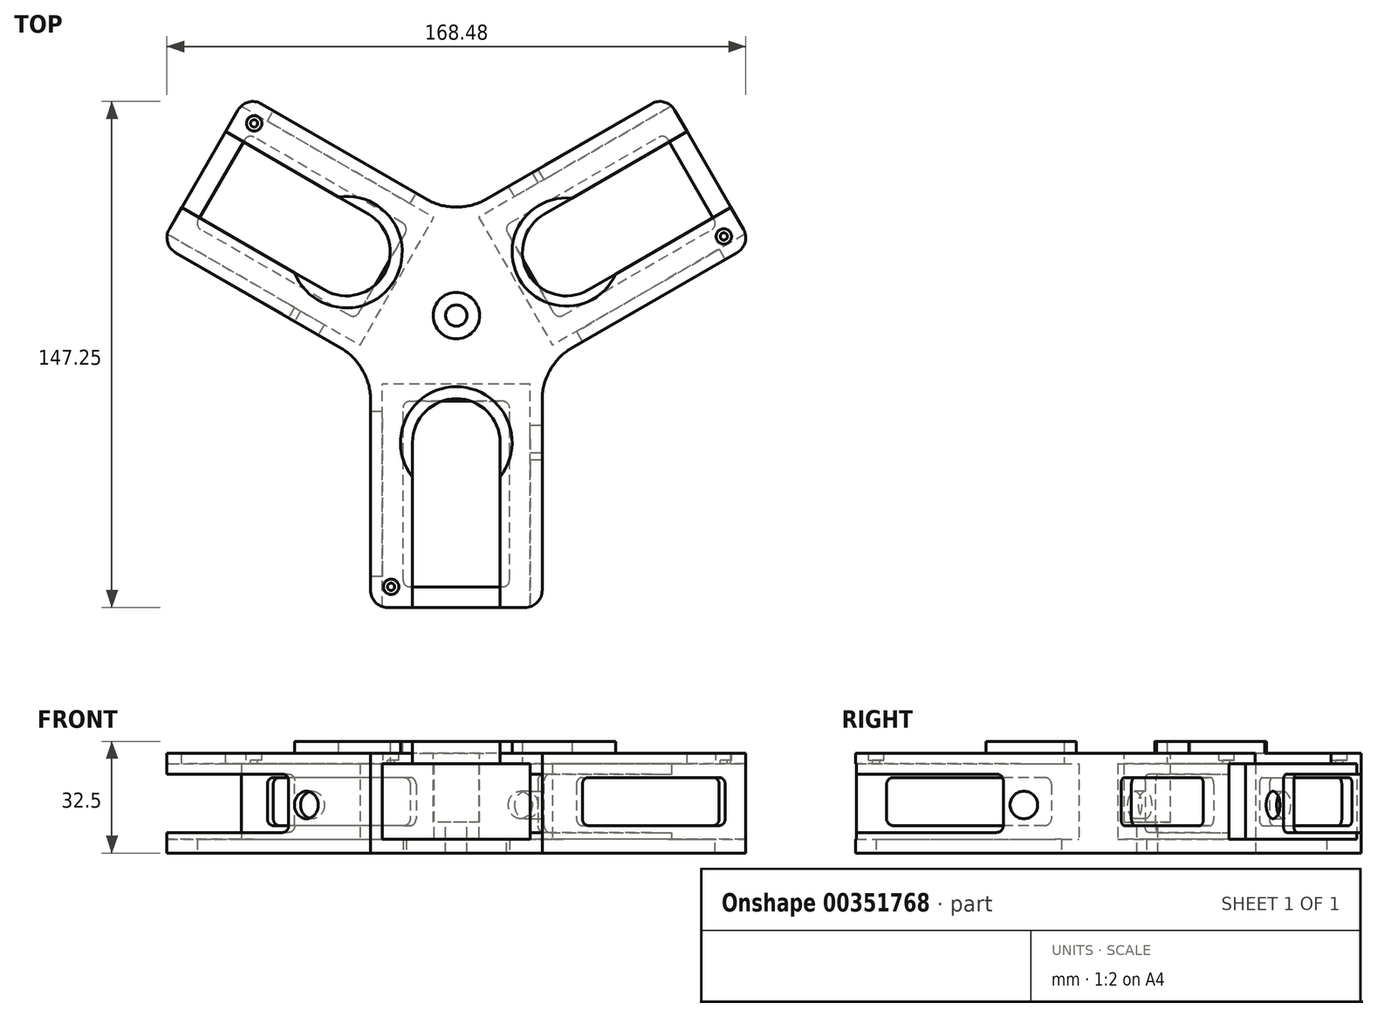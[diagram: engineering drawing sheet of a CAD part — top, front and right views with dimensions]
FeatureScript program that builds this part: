
annotation { "Feature Type Name" : "Feature", "Feature Type Description" : "" }
export const myFeature = defineFeature(function(context is Context, id is Id, definition is map)
    precondition{}
    {
        {
            var Q0;
            Q0=qCreatedBy(makeId("Top.planeOp"),FACE);
            var sketch = newSketch(context, id + "F0", { "sketchPlane" : qUnion([Q0])});
            skCircle(sketch, "E0.cCircle", {"center": v(0, 0) * mm, "radius": 18.48 * mm, "construction": true});
            skLineSegment(sketch, "E0.0", {"start": v(-32, 18.48) * mm, "end": v(32, 18.48) * mm, "construction": true});
            skLineSegment(sketch, "E0.1", {"start": v(32, 18.48) * mm, "end": v(0, -36.95) * mm, "construction": true});
            skLineSegment(sketch, "E0.2", {"start": v(0, -36.95) * mm, "end": v(-32, 18.48) * mm, "construction": true});
            skPoint(sketch, "E0.0.midPoint", {"position": v(0, 18.48) * mm});
            skLineSegment(sketch, "E1.bottom", {"start": v(21.5, -84.95) * mm, "end": v(-21.5, -84.95) * mm});
            skLineSegment(sketch, "E1.top", {"start": v(21.5, -19.95) * mm, "end": v(-21.5, -19.95) * mm});
            skLineSegment(sketch, "E1.left", {"start": v(21.5, -84.95) * mm, "end": v(21.5, -19.95) * mm});
            skLineSegment(sketch, "E1.right", {"start": v(-21.5, -84.95) * mm, "end": v(-21.5, -19.95) * mm});
            skPoint(sketch, "E1.middle", {"position": v(0, -52.45) * mm});
            skLineSegment(sketch, "E2.1.0", {"start": v(84.32, 23.86) * mm, "end": v(28.03, -8.64) * mm});
            skLineSegment(sketch, "E2.1.1", {"start": v(6.53, 28.6) * mm, "end": v(28.03, -8.64) * mm});
            skLineSegment(sketch, "E2.1.2", {"start": v(62.82, 61.1) * mm, "end": v(6.53, 28.6) * mm});
            skLineSegment(sketch, "E2.1.3", {"start": v(62.82, 61.1) * mm, "end": v(84.32, 23.86) * mm});
            skLineSegment(sketch, "E2.2.0", {"start": v(-62.82, 61.1) * mm, "end": v(-6.53, 28.6) * mm});
            skLineSegment(sketch, "E2.2.1", {"start": v(-28.03, -8.64) * mm, "end": v(-6.53, 28.6) * mm});
            skLineSegment(sketch, "E2.2.2", {"start": v(-84.32, 23.86) * mm, "end": v(-28.03, -8.64) * mm});
            skLineSegment(sketch, "E2.2.3", {"start": v(-84.32, 23.86) * mm, "end": v(-62.82, 61.1) * mm});
            skPoint(sketch, "E3.centerSnap0", {"position": v(0, -19.95) * mm});
            skCircle(sketch, "E4", {"center": v(0, -36.95) * mm, "radius": 12.75 * mm});
            skCircle(sketch, "E5", {"center": v(32, 18.48) * mm, "radius": 12.75 * mm});
            skCircle(sketch, "E6", {"center": v(-32, 18.48) * mm, "radius": 12.75 * mm});
            skLineSegment(sketch, "E7.0", {"start": v(61.07, 64.13) * mm, "end": v(4.78, 31.63) * mm});
            skLineSegment(sketch, "E7.2", {"start": v(86.07, 20.82) * mm, "end": v(29.78, -11.68) * mm});
            skLineSegment(sketch, "E8.0", {"start": v(-61.07, 64.13) * mm, "end": v(-4.78, 31.63) * mm});
            skLineSegment(sketch, "E8.2", {"start": v(-86.07, 20.82) * mm, "end": v(-29.78, -11.68) * mm});
            skLineSegment(sketch, "E9.0", {"start": v(25, -84.95) * mm, "end": v(25, -19.95) * mm});
            skLineSegment(sketch, "E9.2", {"start": v(-25, -84.95) * mm, "end": v(-25, -19.95) * mm});
            skLineSegment(sketch, "E10", {"start": v(4.78, 31.63) * mm, "end": v(-4.78, 31.63) * mm});
            skLineSegment(sketch, "E11", {"start": v(29.78, -11.68) * mm, "end": v(25, -19.95) * mm});
            skLineSegment(sketch, "E12", {"start": v(-29.78, -11.68) * mm, "end": v(-25, -19.95) * mm});
            skCircle(sketch, "E13", {"center": v(0, 0) * mm, "radius": 3.1 * mm});
            skLineSegment(sketch, "E14", {"start": v(-62.82, 61.1) * mm, "end": v(-61.07, 64.13) * mm});
            skLineSegment(sketch, "E15", {"start": v(-84.32, 23.86) * mm, "end": v(-86.07, 20.82) * mm});
            skLineSegment(sketch, "E16", {"start": v(-21.5, -84.95) * mm, "end": v(-25, -84.95) * mm});
            skLineSegment(sketch, "E17", {"start": v(21.5, -84.95) * mm, "end": v(25, -84.95) * mm});
            skLineSegment(sketch, "E18", {"start": v(62.82, 61.1) * mm, "end": v(61.07, 64.13) * mm});
            skLineSegment(sketch, "E19", {"start": v(84.32, 23.86) * mm, "end": v(86.07, 20.82) * mm});
            skSolve(sketch);
        }
        {
            var Q0;
            Q0=makeQuery(id+"F0.imprint","IMPRINT",FACE,{"disambiguationData":[TD([[makeQuery(id+"F0.imprint","IMPRINT",EDGE,{"derivedFrom":sQuery(id+"F0.wireOp",EDGE,"E1.top")}),-1.0]])]});
            var Q1;
            Q1=makeQuery(id+"F0.imprint","IMPRINT",FACE,{"disambiguationData":[TD([[makeQuery(id+"F0.imprint","IMPRINT",EDGE,{"derivedFrom":sQuery(id+"F0.wireOp",EDGE,"E2.2.0")}),-1.0]])]});
            var Q2;
            Q2=makeQuery(id+"F0.imprint","IMPRINT",FACE,{"disambiguationData":[TD([[makeQuery(id+"F0.imprint","IMPRINT",EDGE,{"derivedFrom":sQuery(id+"F0.wireOp",EDGE,"E6")}),1.0]])]});
            var Q3;
            Q3=makeQuery(id+"F0.imprint","IMPRINT",FACE,{"disambiguationData":[TD([[makeQuery(id+"F0.imprint","IMPRINT",EDGE,{"derivedFrom":sQuery(id+"F0.wireOp",EDGE,"E5")}),1.0]])]});
            var Q4;
            Q4=makeQuery(id+"F0.imprint","IMPRINT",FACE,{"disambiguationData":[TD([[makeQuery(id+"F0.imprint","IMPRINT",EDGE,{"derivedFrom":sQuery(id+"F0.wireOp",EDGE,"E2.1.0")}),-1.0]])]});
            var Q5;
            Q5=makeQuery(id+"F0.imprint","IMPRINT",FACE,{"disambiguationData":[TD([[makeQuery(id+"F0.imprint","IMPRINT",EDGE,{"derivedFrom":sQuery(id+"F0.wireOp",EDGE,"E1.bottom")}),-1.0]])]});
            var Q6;
            Q6=makeQuery(id+"F0.imprint","IMPRINT",FACE,{"disambiguationData":[TD([[makeQuery(id+"F0.imprint","IMPRINT",EDGE,{"derivedFrom":sQuery(id+"F0.wireOp",EDGE,"E4")}),1.0]])]});
            var Q7;
            Q7=makeQuery(id+"F0.imprint","IMPRINT",FACE,{"disambiguationData":[TD([[makeQuery(id+"F0.imprint","IMPRINT",EDGE,{"derivedFrom":sQuery(id+"F0.wireOp",EDGE,"E1.bottom")}),1.0]])]});
            var Q8;
            Q8=makeQuery(id+"F0.imprint","IMPRINT",FACE,{"disambiguationData":[TD([[makeQuery(id+"F0.imprint","IMPRINT",EDGE,{"derivedFrom":sQuery(id+"F0.wireOp",EDGE,"E2.1.3")}),1.0]])]});
            var Q9;
            Q9=makeQuery(id+"F0.imprint","IMPRINT",FACE,{"disambiguationData":[TD([[makeQuery(id+"F0.imprint","IMPRINT",EDGE,{"derivedFrom":sQuery(id+"F0.wireOp",EDGE,"E2.2.3")}),1.0]])]});
            extrude(context, id + "F1", {"entities" : qUnion([Q0, Q1, Q2, Q3, Q4, Q5, Q6, Q7, Q8, Q9]), "oppositeDirection" : true, "depth" : 4 * mm, "offsetDistance" : 25 * mm});
        }
        {
            var Q0;
            Q0=makeQuery(id+"F0.imprint","IMPRINT",FACE,{"disambiguationData":[TD([[makeQuery(id+"F0.imprint","IMPRINT",EDGE,{"derivedFrom":sQuery(id+"F0.wireOp",EDGE,"E1.top")}),-1.0]])]});
            extrude(context, id + "F2", {"entities" : qUnion([Q0]), "operationType" : NewBodyOperationType.ADD, "depth" : 25 * mm, "offsetDistance" : 25 * mm});
        }
        {
            var Q0;
            Q0=makeQuery(id+"F0.imprint","IMPRINT",FACE,{"disambiguationData":[TD([[makeQuery(id+"F0.imprint","IMPRINT",EDGE,{"derivedFrom":sQuery(id+"F0.wireOp",EDGE,"E1.bottom")}),-1.0]])]});
            var Q1;
            Q1=makeQuery(id+"F0.imprint","IMPRINT",FACE,{"disambiguationData":[TD([[makeQuery(id+"F0.imprint","IMPRINT",EDGE,{"derivedFrom":sQuery(id+"F0.wireOp",EDGE,"E2.2.0")}),-1.0]])]});
            var Q2;
            Q2=makeQuery(id+"F0.imprint","IMPRINT",FACE,{"disambiguationData":[TD([[makeQuery(id+"F0.imprint","IMPRINT",EDGE,{"derivedFrom":sQuery(id+"F0.wireOp",EDGE,"E2.1.0")}),-1.0]])]});
            extrude(context, id + "F3", {"entities" : qUnion([Q0, Q1, Q2]), "operationType" : NewBodyOperationType.ADD, "depth" : 25 * mm, "offsetDistance" : 25 * mm, "hasSecondDirection" : true, "secondDirectionOppositeDirection" : false, "secondDirectionDepth" : 22 * mm});
        }
        {
            var Q0;
            Q0=makeQuery(id+"F0.imprint","IMPRINT",FACE,{"disambiguationData":[TD([[makeQuery(id+"F0.imprint","IMPRINT",EDGE,{"derivedFrom":sQuery(id+"F0.wireOp",EDGE,"E5")}),1.0]])]});
            var Q1;
            Q1=makeQuery(id+"F0.imprint","IMPRINT",FACE,{"disambiguationData":[TD([[makeQuery(id+"F0.imprint","IMPRINT",EDGE,{"derivedFrom":sQuery(id+"F0.wireOp",EDGE,"E6")}),1.0]])]});
            var Q2;
            Q2=makeQuery(id+"F0.imprint","IMPRINT",FACE,{"disambiguationData":[TD([[makeQuery(id+"F0.imprint","IMPRINT",EDGE,{"derivedFrom":sQuery(id+"F0.wireOp",EDGE,"E4")}),1.0]])]});
            extrude(context, id + "F4", {"entities" : qUnion([Q0, Q1, Q2]), "operationType" : NewBodyOperationType.REMOVE, "depth" : 36.1 * mm, "offsetDistance" : 25 * mm, "hasSecondDirection" : true, "secondDirectionOppositeDirection" : false, "secondDirectionDepth" : 12.2 * mm});
        }
        {
            var Q0;
            {var subQ0=sQuery(id+"F0.wireOp",EDGE,"E2.2.2");var subQ1=sQuery(id+"F0.wireOp",EDGE,"E2.2.1");var subQ2=sQuery(id+"F0.wireOp",EDGE,"E2.2.0");var subQ3=sQuery(id+"F0.wireOp",EDGE,"E2.1.2");var subQ4=sQuery(id+"F0.wireOp",EDGE,"E2.1.1");var subQ5=sQuery(id+"F0.wireOp",EDGE,"E2.1.0");var subQ6=sQuery(id+"F0.wireOp",EDGE,"E1.right");var subQ7=sQuery(id+"F0.wireOp",EDGE,"E1.left");var subQ8=sQuery(id+"F0.wireOp",EDGE,"E1.top");Q0=makeQuery(id+"F3.boolean.opBoolean","MERGE",FACE,{"derivedFrom":[makeQuery(id+"F2.opExtrude","CAP_FACE",FACE,{"disambiguationData":[OSD([subQ8,subQ7,subQ6,subQ5,subQ4,subQ3,subQ2,subQ1,subQ0,sQuery(id+"F0.wireOp",EDGE,"E7.0"),sQuery(id+"F0.wireOp",EDGE,"E7.1"),sQuery(id+"F0.wireOp",EDGE,"E7.2"),sQuery(id+"F0.wireOp",EDGE,"E8.0"),sQuery(id+"F0.wireOp",EDGE,"E8.1"),sQuery(id+"F0.wireOp",EDGE,"E8.2"),sQuery(id+"F0.wireOp",EDGE,"E9.0"),sQuery(id+"F0.wireOp",EDGE,"E9.1"),sQuery(id+"F0.wireOp",EDGE,"E9.2"),sQuery(id+"F0.wireOp",EDGE,"E10"),sQuery(id+"F0.wireOp",EDGE,"E11"),sQuery(id+"F0.wireOp",EDGE,"E12"),sQuery(id+"F0.wireOp",EDGE,"jiN8x03o-aMMn-jMTH-HvWz-tqMVP37OVDIm"),sQuery(id+"F0.wireOp",EDGE,"EKPgnR2F-pnn3-6EDa-x4Kd-Pkry5YZrHWNk"),sQuery(id+"F0.wireOp",EDGE,"n5eVLuFF-JwKT-QSBh-8ASv-iFnnVuZWaxG4"),sQuery(id+"F0.wireOp",EDGE,"HnI92CDr-kPty-4Z3F-qDl1-UzYuS8kZJhd5"),sQuery(id+"F0.wireOp",EDGE,"Mza90nwJ-3rcs-2YEg-8f4p-QPBBZ3gxiD8u"),sQuery(id+"F0.wireOp",EDGE,"szRdEE3T-eoAc-AhTw-RHdj-YrhbBiVasdUm"),sQuery(id+"F0.wireOp",EDGE,"E13")])],"isStart":false}),makeQuery(id+"F3.opExtrude","CAP_FACE",FACE,{"disambiguationData":[OSD([sQuery(id+"F0.wireOp",EDGE,"E1.bottom"),subQ8,subQ7,subQ6,sQuery(id+"F0.wireOp",EDGE,"E4")])],"isStart":false}),makeQuery(id+"F3.opExtrude","CAP_FACE",FACE,{"disambiguationData":[OSD([subQ5,subQ4,subQ3,sQuery(id+"F0.wireOp",EDGE,"E2.1.3"),sQuery(id+"F0.wireOp",EDGE,"E5")])],"isStart":false}),makeQuery(id+"F3.opExtrude","CAP_FACE",FACE,{"disambiguationData":[OSD([subQ2,subQ1,subQ0,sQuery(id+"F0.wireOp",EDGE,"E2.2.3"),sQuery(id+"F0.wireOp",EDGE,"E6")])],"isStart":false})]});}
            var sketch = newSketch(context, id + "F5", { "sketchPlane" : qUnion([Q0])});
            skLineSegment(sketch, "E20", {"start": v(12.75, -36.95) * mm, "end": v(12.75, -84.95) * mm});
            skLineSegment(sketch, "E21", {"start": v(-12.75, -36.95) * mm, "end": v(-12.75, -84.95) * mm});
            skLineSegment(sketch, "E22.1.0", {"start": v(38.37, 7.43) * mm, "end": v(79.94, 31.43) * mm});
            skLineSegment(sketch, "E22.1.1", {"start": v(25.62, 29.52) * mm, "end": v(67.2, 53.52) * mm});
            skLineSegment(sketch, "E22.2.0", {"start": v(-25.62, 29.52) * mm, "end": v(-67.2, 53.52) * mm});
            skLineSegment(sketch, "E22.2.1", {"start": v(-38.37, 7.43) * mm, "end": v(-79.94, 31.43) * mm});
            skPoint(sketch, "E22.center", {"position": v(0, 0) * mm});
            skArc(sketch, "E23.0", {"start": v(33.63, 34.14) * mm, "mid": v(18.36, 10.6) * mm, "end": v(46.38, 12.06) * mm});
            skArc(sketch, "E24.0", {"start": v(-47.1, 12.47) * mm, "mid": v(-17.93, 10.35) * mm, "end": v(-34.35, 34.55) * mm});
            skArc(sketch, "E25.0", {"start": v(12.75, -47.03) * mm, "mid": v(0, -20.7) * mm, "end": v(-12.75, -47.03) * mm});
            skCircle(sketch, "E26", {"center": v(-19, -78.95) * mm, "radius": 4.86 * mm});
            skCircle(sketch, "E27.1.0", {"center": v(77.87, 23.02) * mm, "radius": 4.86 * mm});
            skCircle(sketch, "E27.2.0", {"center": v(-58.87, 55.93) * mm, "radius": 4.86 * mm});
            skSolve(sketch);
        }
        {
            var Q0;
            {var subQ0=sQuery(id+"F5.wireOp",EDGE,"E22.2.0");Q0=makeQuery(id+"F5.imprint","IMPRINT",FACE,{"disambiguationData":[TD([[makeQuery(id+"F5.imprint","IMPRINT",EDGE,{"derivedFrom":subQ0}),1.0]])]});}
            var Q1;
            {var subQ0=sQuery(id+"F5.wireOp",EDGE,"E22.1.0");Q1=makeQuery(id+"F5.imprint","IMPRINT",FACE,{"disambiguationData":[TD([[makeQuery(id+"F5.imprint","IMPRINT",EDGE,{"derivedFrom":subQ0}),1.0]])]});}
            var Q2;
            {var subQ0=sQuery(id+"F5.wireOp",EDGE,"E20");Q2=makeQuery(id+"F5.imprint","IMPRINT",FACE,{"disambiguationData":[TD([[makeQuery(id+"F5.imprint","IMPRINT",EDGE,{"derivedFrom":subQ0}),-1.0]])]});}
            extrude(context, id + "F6", {"entities" : qUnion([Q0, Q1, Q2]), "operationType" : NewBodyOperationType.REMOVE, "oppositeDirection" : true, "depth" : 13.4 * mm, "offsetDistance" : 25 * mm});
        }
        {
            var Q0;
            {var subQ32=sQuery(id+"F5.wireOp",EDGE,"E24.0");Q0=makeQuery(id+"F5.imprint","IMPRINT",FACE,{"disambiguationData":[TD([[makeQuery(id+"F5.imprint","IMPRINT",EDGE,{"derivedFrom":subQ32}),1.0]])]});}
            var Q1;
            {var subQ32=sQuery(id+"F5.wireOp",EDGE,"E23.0");Q1=makeQuery(id+"F5.imprint","IMPRINT",FACE,{"disambiguationData":[TD([[makeQuery(id+"F5.imprint","IMPRINT",EDGE,{"derivedFrom":subQ32}),1.0]])]});}
            var Q2;
            {var subQ32=sQuery(id+"F5.wireOp",EDGE,"E25.0");Q2=makeQuery(id+"F5.imprint","IMPRINT",FACE,{"disambiguationData":[TD([[makeQuery(id+"F5.imprint","IMPRINT",EDGE,{"derivedFrom":subQ32}),1.0]])]});}
            extrude(context, id + "F7", {"entities" : qUnion([Q0, Q1, Q2]), "operationType" : NewBodyOperationType.ADD, "depth" : 3.5 * mm, "offsetDistance" : 25 * mm});
        }
        {
            var Q0;
            Q0=makeQuery(id+"F1.opExtrude","CAP_FACE",FACE,{"disambiguationData":[OSD([sQuery(id+"F0.wireOp",EDGE,"E7.0"),sQuery(id+"F0.wireOp",EDGE,"E7.1"),sQuery(id+"F0.wireOp",EDGE,"E7.2"),sQuery(id+"F0.wireOp",EDGE,"E8.0"),sQuery(id+"F0.wireOp",EDGE,"E8.1"),sQuery(id+"F0.wireOp",EDGE,"E8.2"),sQuery(id+"F0.wireOp",EDGE,"E9.0"),sQuery(id+"F0.wireOp",EDGE,"E9.1"),sQuery(id+"F0.wireOp",EDGE,"E9.2"),sQuery(id+"F0.wireOp",EDGE,"E10"),sQuery(id+"F0.wireOp",EDGE,"E11"),sQuery(id+"F0.wireOp",EDGE,"E12"),sQuery(id+"F0.wireOp",EDGE,"E13")])],"isStart":false});
            var sketch = newSketch(context, id + "F8", { "sketchPlane" : qUnion([Q0])});
            skLineSegment(sketch, "E28.bottom", {"start": v(-15.5, 24.95) * mm, "end": v(15.5, 24.95) * mm});
            skLineSegment(sketch, "E28.top", {"start": v(-15.5, 78.95) * mm, "end": v(15.5, 78.95) * mm});
            skLineSegment(sketch, "E28.left", {"start": v(-15.5, 24.95) * mm, "end": v(-15.5, 78.95) * mm});
            skLineSegment(sketch, "E28.right", {"start": v(15.5, 24.95) * mm, "end": v(15.5, 78.95) * mm});
            skLineSegment(sketch, "E29.1.0", {"start": v(-29.36, 0.95) * mm, "end": v(-76.12, -26.05) * mm});
            skLineSegment(sketch, "E29.1.1", {"start": v(-60.62, -52.9) * mm, "end": v(-76.12, -26.05) * mm});
            skLineSegment(sketch, "E29.1.2", {"start": v(-13.86, -25.9) * mm, "end": v(-60.62, -52.9) * mm});
            skLineSegment(sketch, "E29.1.3", {"start": v(-13.86, -25.9) * mm, "end": v(-29.36, 0.95) * mm});
            skLineSegment(sketch, "E29.2.0", {"start": v(13.86, -25.9) * mm, "end": v(60.62, -52.9) * mm});
            skLineSegment(sketch, "E29.2.1", {"start": v(76.12, -26.05) * mm, "end": v(60.62, -52.9) * mm});
            skLineSegment(sketch, "E29.2.2", {"start": v(29.36, 0.95) * mm, "end": v(76.12, -26.05) * mm});
            skLineSegment(sketch, "E29.2.3", {"start": v(29.36, 0.95) * mm, "end": v(13.86, -25.9) * mm});
            skPoint(sketch, "E29.center", {"position": v(0, 0) * mm});
            skSolve(sketch);
        }
        {
            var Q0;
            Q0=makeQuery(id+"F8.imprint","IMPRINT",FACE,{"disambiguationData":[TD([[makeQuery(id+"F8.imprint","IMPRINT",EDGE,{"derivedFrom":sQuery(id+"F8.wireOp",EDGE,"E29.2.0")}),1.0]])]});
            var Q1;
            Q1=makeQuery(id+"F8.imprint","IMPRINT",FACE,{"disambiguationData":[TD([[makeQuery(id+"F8.imprint","IMPRINT",EDGE,{"derivedFrom":sQuery(id+"F8.wireOp",EDGE,"E28.bottom")}),1.0]])]});
            var Q2;
            Q2=makeQuery(id+"F8.imprint","IMPRINT",FACE,{"disambiguationData":[TD([[makeQuery(id+"F8.imprint","IMPRINT",EDGE,{"derivedFrom":sQuery(id+"F8.wireOp",EDGE,"E29.1.0")}),1.0]])]});
            extrude(context, id + "F9", {"entities" : qUnion([Q0, Q1, Q2]), "operationType" : NewBodyOperationType.REMOVE, "oppositeDirection" : true, "depth" : 17 * mm, "offsetDistance" : 25 * mm});
        }
        {
            var Q0;
            {var subQ0=sQuery(id+"F0.wireOp",EDGE,"E7.0");Q0=makeQuery(id+"F2.boolean.opBoolean","MERGE",FACE,{"derivedFrom":[makeQuery(id+"F1.opExtrude","SWEPT_FACE",FACE,{"disambiguationData":[OSD([subQ0])]}),makeQuery(id+"F2.opExtrude","SWEPT_FACE",FACE,{"disambiguationData":[OSD([subQ0])]})]});}
            var sketch = newSketch(context, id + "F10", { "sketchPlane" : qUnion([Q0])});
            skLineSegment(sketch, "E30.bottom", {"start": v(-84.95, 19) * mm, "end": v(-41.95, 19) * mm});
            skLineSegment(sketch, "E30.top", {"start": v(-84.95, 2) * mm, "end": v(-41.95, 2) * mm});
            skLineSegment(sketch, "E30.left", {"start": v(-84.95, 19) * mm, "end": v(-84.95, 2) * mm});
            skLineSegment(sketch, "E30.right", {"start": v(-41.95, 19) * mm, "end": v(-41.95, 2) * mm});
            skCircle(sketch, "E31", {"center": v(-35.95, 10) * mm, "radius": 4 * mm});
            skSolve(sketch);
        }
        {
            var Q0;
            {var subQ0=sQuery(id+"F0.wireOp",EDGE,"E8.2");Q0=makeQuery(id+"F2.boolean.opBoolean","MERGE",FACE,{"derivedFrom":[makeQuery(id+"F1.opExtrude","SWEPT_FACE",FACE,{"disambiguationData":[OSD([subQ0])]}),makeQuery(id+"F2.opExtrude","SWEPT_FACE",FACE,{"disambiguationData":[OSD([subQ0])]})]});}
            var sketch = newSketch(context, id + "F11", { "sketchPlane" : qUnion([Q0])});
            skLineSegment(sketch, "E32.bottom", {"start": v(-84.95, 19) * mm, "end": v(-41.95, 19) * mm});
            skLineSegment(sketch, "E32.top", {"start": v(-84.95, 2) * mm, "end": v(-41.95, 2) * mm});
            skLineSegment(sketch, "E32.left", {"start": v(-84.95, 19) * mm, "end": v(-84.95, 2) * mm});
            skLineSegment(sketch, "E32.right", {"start": v(-41.95, 19) * mm, "end": v(-41.95, 2) * mm});
            skCircle(sketch, "E33", {"center": v(-35.95, 10) * mm, "radius": 4 * mm});
            skSolve(sketch);
        }
        {
            var Q0;
            {var subQ0=sQuery(id+"F0.wireOp",EDGE,"E9.0");Q0=makeQuery(id+"F2.boolean.opBoolean","MERGE",FACE,{"derivedFrom":[makeQuery(id+"F1.opExtrude","SWEPT_FACE",FACE,{"disambiguationData":[OSD([subQ0])]}),makeQuery(id+"F2.opExtrude","SWEPT_FACE",FACE,{"disambiguationData":[OSD([subQ0])]})]});}
            var sketch = newSketch(context, id + "F12", { "sketchPlane" : qUnion([Q0])});
            skLineSegment(sketch, "E34.bottom", {"start": v(-84.95, 19) * mm, "end": v(-41.95, 19) * mm});
            skLineSegment(sketch, "E34.top", {"start": v(-84.95, 2) * mm, "end": v(-41.95, 2) * mm});
            skLineSegment(sketch, "E34.left", {"start": v(-84.95, 19) * mm, "end": v(-84.95, 2) * mm});
            skLineSegment(sketch, "E34.right", {"start": v(-41.95, 19) * mm, "end": v(-41.95, 2) * mm});
            skCircle(sketch, "E35", {"center": v(-35.95, 10) * mm, "radius": 4 * mm});
            skSolve(sketch);
        }
        {
            var Q0;
            Q0=makeQuery(id+"F10.imprint","IMPRINT",FACE,{"disambiguationData":[TD([[makeQuery(id+"F10.imprint","IMPRINT",EDGE,{"derivedFrom":sQuery(id+"F10.wireOp",EDGE,"E30.bottom")}),-1.0]])]});
            var Q1;
            Q1=makeQuery(id+"F10.imprint","IMPRINT",FACE,{"disambiguationData":[TD([[makeQuery(id+"F10.imprint","IMPRINT",EDGE,{"derivedFrom":sQuery(id+"F10.wireOp",EDGE,"E31")}),1.0]])]});
            extrude(context, id + "F13", {"entities" : qUnion([Q0, Q1]), "operationType" : NewBodyOperationType.REMOVE, "oppositeDirection" : true, "depth" : 25 * mm, "offsetDistance" : 25 * mm});
        }
        {
            var Q0;
            Q0=makeQuery(id+"F11.imprint","IMPRINT",FACE,{"disambiguationData":[TD([[makeQuery(id+"F11.imprint","IMPRINT",EDGE,{"derivedFrom":sQuery(id+"F11.wireOp",EDGE,"E32.bottom")}),-1.0]])]});
            var Q1;
            Q1=makeQuery(id+"F11.imprint","IMPRINT",FACE,{"disambiguationData":[TD([[makeQuery(id+"F11.imprint","IMPRINT",EDGE,{"derivedFrom":sQuery(id+"F11.wireOp",EDGE,"E33")}),1.0]])]});
            extrude(context, id + "F14", {"entities" : qUnion([Q0, Q1]), "operationType" : NewBodyOperationType.REMOVE, "oppositeDirection" : true, "depth" : 25 * mm, "offsetDistance" : 25 * mm});
        }
        {
            var Q0;
            Q0=makeQuery(id+"F12.imprint","IMPRINT",FACE,{"disambiguationData":[TD([[makeQuery(id+"F12.imprint","IMPRINT",EDGE,{"derivedFrom":sQuery(id+"F12.wireOp",EDGE,"E34.bottom")}),-1.0]])]});
            var Q1;
            Q1=makeQuery(id+"F12.imprint","IMPRINT",FACE,{"disambiguationData":[TD([[makeQuery(id+"F12.imprint","IMPRINT",EDGE,{"derivedFrom":sQuery(id+"F12.wireOp",EDGE,"E35")}),1.0]])]});
            extrude(context, id + "F15", {"entities" : qUnion([Q0, Q1]), "operationType" : NewBodyOperationType.REMOVE, "oppositeDirection" : true, "depth" : 25 * mm, "offsetDistance" : 25 * mm});
        }
        {
            var Q0;
            {var subQ0=sQuery(id+"F0.wireOp",EDGE,"E9.2");Q0=makeQuery(id+"F2.boolean.opBoolean","MERGE",FACE,{"derivedFrom":[makeQuery(id+"F1.opExtrude","SWEPT_FACE",FACE,{"disambiguationData":[OSD([subQ0])]}),makeQuery(id+"F2.opExtrude","SWEPT_FACE",FACE,{"disambiguationData":[OSD([subQ0])]})]});}
            var sketch = newSketch(context, id + "F16", { "sketchPlane" : qUnion([Q0])});
            skLineSegment(sketch, "E36.bottom", {"start": v(27.95, 18) * mm, "end": v(75.95, 18) * mm});
            skLineSegment(sketch, "E36.top", {"start": v(27.95, 4) * mm, "end": v(75.95, 4) * mm});
            skLineSegment(sketch, "E36.left", {"start": v(27.95, 18) * mm, "end": v(27.95, 4) * mm});
            skLineSegment(sketch, "E36.right", {"start": v(75.95, 18) * mm, "end": v(75.95, 4) * mm});
            skSolve(sketch);
        }
        {
            var Q0;
            {var subQ0=sQuery(id+"F0.wireOp",EDGE,"E7.2");Q0=makeQuery(id+"F2.boolean.opBoolean","MERGE",FACE,{"derivedFrom":[makeQuery(id+"F1.opExtrude","SWEPT_FACE",FACE,{"disambiguationData":[OSD([subQ0])]}),makeQuery(id+"F2.opExtrude","SWEPT_FACE",FACE,{"disambiguationData":[OSD([subQ0])]})]});}
            var sketch = newSketch(context, id + "F17", { "sketchPlane" : qUnion([Q0])});
            skLineSegment(sketch, "E37.bottom", {"start": v(27.95, 18) * mm, "end": v(75.95, 18) * mm});
            skLineSegment(sketch, "E37.top", {"start": v(27.95, 4) * mm, "end": v(75.95, 4) * mm});
            skLineSegment(sketch, "E37.left", {"start": v(27.95, 18) * mm, "end": v(27.95, 4) * mm});
            skLineSegment(sketch, "E37.right", {"start": v(75.95, 18) * mm, "end": v(75.95, 4) * mm});
            skSolve(sketch);
        }
        {
            var Q0;
            {var subQ0=sQuery(id+"F0.wireOp",EDGE,"E8.0");Q0=makeQuery(id+"F2.boolean.opBoolean","MERGE",FACE,{"derivedFrom":[makeQuery(id+"F1.opExtrude","SWEPT_FACE",FACE,{"disambiguationData":[OSD([subQ0])]}),makeQuery(id+"F2.opExtrude","SWEPT_FACE",FACE,{"disambiguationData":[OSD([subQ0])]})]});}
            var sketch = newSketch(context, id + "F18", { "sketchPlane" : qUnion([Q0])});
            skLineSegment(sketch, "E38.bottom", {"start": v(27.95, 18) * mm, "end": v(75.95, 18) * mm});
            skLineSegment(sketch, "E38.top", {"start": v(27.95, 4) * mm, "end": v(75.95, 4) * mm});
            skLineSegment(sketch, "E38.left", {"start": v(27.95, 18) * mm, "end": v(27.95, 4) * mm});
            skLineSegment(sketch, "E38.right", {"start": v(75.95, 18) * mm, "end": v(75.95, 4) * mm});
            skSolve(sketch);
        }
        {
            var Q0;
            Q0=makeQuery(id+"F16.imprint","IMPRINT",FACE,{"disambiguationData":[TD([[makeQuery(id+"F16.imprint","IMPRINT",EDGE,{"derivedFrom":sQuery(id+"F16.wireOp",EDGE,"E36.bottom")}),-1.0]])]});
            extrude(context, id + "F19", {"entities" : qUnion([Q0]), "operationType" : NewBodyOperationType.REMOVE, "oppositeDirection" : true, "depth" : 25 * mm, "offsetDistance" : 25 * mm});
        }
        {
            var Q0;
            Q0=makeQuery(id+"F17.imprint","IMPRINT",FACE,{"disambiguationData":[TD([[makeQuery(id+"F17.imprint","IMPRINT",EDGE,{"derivedFrom":sQuery(id+"F17.wireOp",EDGE,"E37.bottom")}),-1.0]])]});
            extrude(context, id + "F20", {"entities" : qUnion([Q0]), "operationType" : NewBodyOperationType.REMOVE, "oppositeDirection" : true, "depth" : 25 * mm, "offsetDistance" : 25 * mm});
        }
        {
            var Q0;
            Q0=makeQuery(id+"F18.imprint","IMPRINT",FACE,{"disambiguationData":[TD([[makeQuery(id+"F18.imprint","IMPRINT",EDGE,{"derivedFrom":sQuery(id+"F18.wireOp",EDGE,"E38.bottom")}),-1.0]])]});
            extrude(context, id + "F21", {"entities" : qUnion([Q0]), "operationType" : NewBodyOperationType.REMOVE, "oppositeDirection" : true, "depth" : 25 * mm, "offsetDistance" : 25 * mm});
        }
        {
            var Q0;
            {var subQ0=sQuery(id+"F0.wireOp",EDGE,"E11");var subQ1=sQuery(id+"F0.wireOp",EDGE,"E7.2");Q0=makeQuery(id+"F2.boolean.opBoolean","MERGE",EDGE,{"derivedFrom":[makeQuery(id+"F1.opExtrude","SWEPT_EDGE",EDGE,{"disambiguationData":[OSD([subQ1,subQ0])]}),makeQuery(id+"F2.opExtrude","SWEPT_EDGE",EDGE,{"disambiguationData":[OSD([subQ1,subQ0])]})]});}
            var Q1;
            {var subQ0=sQuery(id+"F0.wireOp",EDGE,"E11");var subQ1=sQuery(id+"F0.wireOp",EDGE,"E9.0");Q1=makeQuery(id+"F2.boolean.opBoolean","MERGE",EDGE,{"derivedFrom":[makeQuery(id+"F1.opExtrude","SWEPT_EDGE",EDGE,{"disambiguationData":[OSD([subQ1,subQ0])]}),makeQuery(id+"F2.opExtrude","SWEPT_EDGE",EDGE,{"disambiguationData":[OSD([subQ1,subQ0])]})]});}
            var Q2;
            {var subQ0=sQuery(id+"F0.wireOp",EDGE,"E10");var subQ1=sQuery(id+"F0.wireOp",EDGE,"E8.0");Q2=makeQuery(id+"F2.boolean.opBoolean","MERGE",EDGE,{"derivedFrom":[makeQuery(id+"F1.opExtrude","SWEPT_EDGE",EDGE,{"disambiguationData":[OSD([subQ1,subQ0])]}),makeQuery(id+"F2.opExtrude","SWEPT_EDGE",EDGE,{"disambiguationData":[OSD([subQ1,subQ0])]})]});}
            var Q3;
            {var subQ0=sQuery(id+"F0.wireOp",EDGE,"E10");var subQ1=sQuery(id+"F0.wireOp",EDGE,"E7.0");Q3=makeQuery(id+"F2.boolean.opBoolean","MERGE",EDGE,{"derivedFrom":[makeQuery(id+"F1.opExtrude","SWEPT_EDGE",EDGE,{"disambiguationData":[OSD([subQ1,subQ0])]}),makeQuery(id+"F2.opExtrude","SWEPT_EDGE",EDGE,{"disambiguationData":[OSD([subQ1,subQ0])]})]});}
            var Q4;
            {var subQ0=sQuery(id+"F0.wireOp",EDGE,"E12");var subQ1=sQuery(id+"F0.wireOp",EDGE,"E9.2");Q4=makeQuery(id+"F2.boolean.opBoolean","MERGE",EDGE,{"derivedFrom":[makeQuery(id+"F1.opExtrude","SWEPT_EDGE",EDGE,{"disambiguationData":[OSD([subQ1,subQ0])]}),makeQuery(id+"F2.opExtrude","SWEPT_EDGE",EDGE,{"disambiguationData":[OSD([subQ1,subQ0])]})]});}
            var Q5;
            {var subQ0=sQuery(id+"F0.wireOp",EDGE,"E12");var subQ1=sQuery(id+"F0.wireOp",EDGE,"E8.2");Q5=makeQuery(id+"F2.boolean.opBoolean","MERGE",EDGE,{"derivedFrom":[makeQuery(id+"F1.opExtrude","SWEPT_EDGE",EDGE,{"disambiguationData":[OSD([subQ1,subQ0])]}),makeQuery(id+"F2.opExtrude","SWEPT_EDGE",EDGE,{"disambiguationData":[OSD([subQ1,subQ0])]})]});}
            fillet(context, id + "F22", {"entities" : qUnion([Q0, Q1, Q2, Q3, Q4, Q5]), "tangentPropagation" : true, "radius" : 16 * mm, "defaultsChanged" : true, "vertexSettings" : [], "allowEdgeOverflow" : false});
        }
        {
            var Q0;
            {var subQ11=sQuery(id+"F0.wireOp",EDGE,"E15");var subQ12=sQuery(id+"F0.wireOp",EDGE,"E8.2");Q0=makeQuery(id+"F14.boolean.opBoolean","SPLIT",EDGE,{"disambiguationData":[TD([makeQuery(id+"F14.opExtrude","SWEPT_FACE",FACE,{"disambiguationData":[OSD([sQuery(id+"F11.wireOp",EDGE,"E32.bottom")])]})])],"derivedFrom":makeQuery(id+"F2.boolean.opBoolean","MERGE",EDGE,{"derivedFrom":[makeQuery(id+"F1.opExtrude","SWEPT_EDGE",EDGE,{"disambiguationData":[OSD([subQ12,subQ11])]}),makeQuery(id+"F2.opExtrude","SWEPT_EDGE",EDGE,{"disambiguationData":[OSD([subQ12,subQ11])]})]})});}
            var Q1;
            {var subQ0=sQuery(id+"F0.wireOp",EDGE,"E8.2");var subQ2=sQuery(id+"F0.wireOp",EDGE,"E15");Q1=makeQuery(id+"F14.boolean.opBoolean","SPLIT",EDGE,{"disambiguationData":[TD([makeQuery(id+"F14.opExtrude","SWEPT_FACE",FACE,{"disambiguationData":[OSD([sQuery(id+"F11.wireOp",EDGE,"E32.top")])]})])],"derivedFrom":makeQuery(id+"F2.boolean.opBoolean","MERGE",EDGE,{"derivedFrom":[makeQuery(id+"F1.opExtrude","SWEPT_EDGE",EDGE,{"disambiguationData":[OSD([subQ0,subQ2])]}),makeQuery(id+"F2.opExtrude","SWEPT_EDGE",EDGE,{"disambiguationData":[OSD([subQ0,subQ2])]})]})});}
            var Q2;
            {var subQ0=sQuery(id+"F0.wireOp",EDGE,"E14");var subQ1=sQuery(id+"F0.wireOp",EDGE,"E8.0");Q2=makeQuery(id+"F2.boolean.opBoolean","MERGE",EDGE,{"derivedFrom":[makeQuery(id+"F1.opExtrude","SWEPT_EDGE",EDGE,{"disambiguationData":[OSD([subQ1,subQ0])]}),makeQuery(id+"F2.opExtrude","SWEPT_EDGE",EDGE,{"disambiguationData":[OSD([subQ1,subQ0])]})]});}
            var Q3;
            {var subQ0=sQuery(id+"F0.wireOp",EDGE,"E16");var subQ1=sQuery(id+"F0.wireOp",EDGE,"E9.2");Q3=makeQuery(id+"F2.boolean.opBoolean","MERGE",EDGE,{"derivedFrom":[makeQuery(id+"F1.opExtrude","SWEPT_EDGE",EDGE,{"disambiguationData":[OSD([subQ1,subQ0])]}),makeQuery(id+"F2.opExtrude","SWEPT_EDGE",EDGE,{"disambiguationData":[OSD([subQ1,subQ0])]})]});}
            var Q4;
            {var subQ8=sQuery(id+"F0.wireOp",EDGE,"E9.0");var subQ9=sQuery(id+"F0.wireOp",EDGE,"E17");Q4=makeQuery(id+"F15.boolean.opBoolean","SPLIT",EDGE,{"disambiguationData":[TD([makeQuery(id+"F15.opExtrude","SWEPT_FACE",FACE,{"disambiguationData":[OSD([sQuery(id+"F12.wireOp",EDGE,"E34.bottom")])]})])],"derivedFrom":makeQuery(id+"F2.boolean.opBoolean","MERGE",EDGE,{"derivedFrom":[makeQuery(id+"F1.opExtrude","SWEPT_EDGE",EDGE,{"disambiguationData":[OSD([subQ8,subQ9])]}),makeQuery(id+"F2.opExtrude","SWEPT_EDGE",EDGE,{"disambiguationData":[OSD([subQ8,subQ9])]})]})});}
            var Q5;
            {var subQ0=sQuery(id+"F0.wireOp",EDGE,"E9.0");var subQ1=sQuery(id+"F0.wireOp",EDGE,"E17");Q5=makeQuery(id+"F15.boolean.opBoolean","SPLIT",EDGE,{"disambiguationData":[TD([makeQuery(id+"F15.opExtrude","SWEPT_FACE",FACE,{"disambiguationData":[OSD([sQuery(id+"F12.wireOp",EDGE,"E34.top")])]})])],"derivedFrom":makeQuery(id+"F2.boolean.opBoolean","MERGE",EDGE,{"derivedFrom":[makeQuery(id+"F1.opExtrude","SWEPT_EDGE",EDGE,{"disambiguationData":[OSD([subQ0,subQ1])]}),makeQuery(id+"F2.opExtrude","SWEPT_EDGE",EDGE,{"disambiguationData":[OSD([subQ0,subQ1])]})]})});}
            var Q6;
            {var subQ0=sQuery(id+"F0.wireOp",EDGE,"E19");var subQ1=sQuery(id+"F0.wireOp",EDGE,"E7.2");Q6=makeQuery(id+"F2.boolean.opBoolean","MERGE",EDGE,{"derivedFrom":[makeQuery(id+"F1.opExtrude","SWEPT_EDGE",EDGE,{"disambiguationData":[OSD([subQ1,subQ0])]}),makeQuery(id+"F2.opExtrude","SWEPT_EDGE",EDGE,{"disambiguationData":[OSD([subQ1,subQ0])]})]});}
            var Q7;
            {var subQ5=sQuery(id+"F0.wireOp",EDGE,"E18");var subQ6=sQuery(id+"F0.wireOp",EDGE,"E7.0");Q7=makeQuery(id+"F13.boolean.opBoolean","SPLIT",EDGE,{"disambiguationData":[TD([makeQuery(id+"F13.opExtrude","SWEPT_FACE",FACE,{"disambiguationData":[OSD([sQuery(id+"F10.wireOp",EDGE,"E30.bottom")])]})])],"derivedFrom":makeQuery(id+"F2.boolean.opBoolean","MERGE",EDGE,{"derivedFrom":[makeQuery(id+"F1.opExtrude","SWEPT_EDGE",EDGE,{"disambiguationData":[OSD([subQ6,subQ5])]}),makeQuery(id+"F2.opExtrude","SWEPT_EDGE",EDGE,{"disambiguationData":[OSD([subQ6,subQ5])]})]})});}
            var Q8;
            {var subQ0=sQuery(id+"F0.wireOp",EDGE,"E7.0");var subQ2=sQuery(id+"F0.wireOp",EDGE,"E18");Q8=makeQuery(id+"F13.boolean.opBoolean","SPLIT",EDGE,{"disambiguationData":[TD([makeQuery(id+"F13.opExtrude","SWEPT_FACE",FACE,{"disambiguationData":[OSD([sQuery(id+"F10.wireOp",EDGE,"E30.top")])]})])],"derivedFrom":makeQuery(id+"F2.boolean.opBoolean","MERGE",EDGE,{"derivedFrom":[makeQuery(id+"F1.opExtrude","SWEPT_EDGE",EDGE,{"disambiguationData":[OSD([subQ0,subQ2])]}),makeQuery(id+"F2.opExtrude","SWEPT_EDGE",EDGE,{"disambiguationData":[OSD([subQ0,subQ2])]})]})});}
            fillet(context, id + "F23", {"entities" : qUnion([Q0, Q1, Q2, Q3, Q4, Q5, Q6, Q7, Q8]), "tangentPropagation" : true, "radius" : 5 * mm, "defaultsChanged" : false, "vertexSettings" : [], "allowEdgeOverflow" : false});
        }
        {
            var Q0;
            Q0=sQuery(id+"F5.wireOp",VERTEX,"E26.center");
            var Q1;
            Q1=sQuery(id+"F5.wireOp",VERTEX,"E27.1.0.center");
            var Q2;
            Q2=sQuery(id+"F5.wireOp",VERTEX,"E27.2.0.center");
            var Q3;
            Q3=makeQuery(id+"F1.opExtrude","SWEPT_BODY",BODY,{"disambiguationData":[OSD([sQuery(id+"F0.wireOp",EDGE,"E1.bottom"),sQuery(id+"F0.wireOp",EDGE,"E2.1.3"),sQuery(id+"F0.wireOp",EDGE,"E2.2.3"),sQuery(id+"F0.wireOp",EDGE,"E7.0"),sQuery(id+"F0.wireOp",EDGE,"E7.2"),sQuery(id+"F0.wireOp",EDGE,"E8.0"),sQuery(id+"F0.wireOp",EDGE,"E8.2"),sQuery(id+"F0.wireOp",EDGE,"E9.0"),sQuery(id+"F0.wireOp",EDGE,"E9.2"),sQuery(id+"F0.wireOp",EDGE,"E10"),sQuery(id+"F0.wireOp",EDGE,"E11"),sQuery(id+"F0.wireOp",EDGE,"E12"),sQuery(id+"F0.wireOp",EDGE,"E13"),sQuery(id+"F0.wireOp",EDGE,"E14"),sQuery(id+"F0.wireOp",EDGE,"E15"),sQuery(id+"F0.wireOp",EDGE,"E16"),sQuery(id+"F0.wireOp",EDGE,"E17"),sQuery(id+"F0.wireOp",EDGE,"E18"),sQuery(id+"F0.wireOp",EDGE,"E19")])]});
            hole(context, id + "F24", {"style" : HoleStyle.C_BORE, "endStyle" : HoleEndStyle.BLIND, "holeDiameter" : 2.1 * mm, "cBoreDiameter" : 4.5 * mm, "cBoreDepth" : 2 * mm, "majorDiameter" : 5 * mm, "holeDepth" : 6 * mm, "isTappedThrough" : true, "tappedDepth" : 12 * mm, "tapClearance" : 3, "locations" : qUnion([Q0, Q1, Q2]), "scope" : qUnion([Q3])});
        }
        {
            var Q0;
            Q0=sQuery(id+"F5.wireOp",VERTEX,"E22.center");
            var Q1;
            Q1=makeQuery(id+"F1.opExtrude","SWEPT_BODY",BODY,{"disambiguationData":[OSD([sQuery(id+"F0.wireOp",EDGE,"E1.bottom"),sQuery(id+"F0.wireOp",EDGE,"E2.1.3"),sQuery(id+"F0.wireOp",EDGE,"E2.2.3"),sQuery(id+"F0.wireOp",EDGE,"E7.0"),sQuery(id+"F0.wireOp",EDGE,"E7.2"),sQuery(id+"F0.wireOp",EDGE,"E8.0"),sQuery(id+"F0.wireOp",EDGE,"E8.2"),sQuery(id+"F0.wireOp",EDGE,"E9.0"),sQuery(id+"F0.wireOp",EDGE,"E9.2"),sQuery(id+"F0.wireOp",EDGE,"E10"),sQuery(id+"F0.wireOp",EDGE,"E11"),sQuery(id+"F0.wireOp",EDGE,"E12"),sQuery(id+"F0.wireOp",EDGE,"E13"),sQuery(id+"F0.wireOp",EDGE,"E14"),sQuery(id+"F0.wireOp",EDGE,"E15"),sQuery(id+"F0.wireOp",EDGE,"E16"),sQuery(id+"F0.wireOp",EDGE,"E17"),sQuery(id+"F0.wireOp",EDGE,"E18"),sQuery(id+"F0.wireOp",EDGE,"E19")])]});
            hole(context, id + "F25", {"style" : HoleStyle.C_BORE, "endStyle" : HoleEndStyle.BLIND, "holeDiameter" : 6.2 * mm, "cBoreDiameter" : 13.5 * mm, "cBoreDepth" : 20 * mm, "majorDiameter" : 5 * mm, "holeDepth" : 30 * mm, "isTappedThrough" : true, "tappedDepth" : 12 * mm, "tapClearance" : 3, "locations" : qUnion([Q0]), "scope" : qUnion([Q1])});
        }
        {
            var Q0;
            Q0=makeQuery(id+"F21.boolean.opBoolean","COPY",EDGE,{"derivedFrom":makeQuery(id+"F21.opExtrude","SWEPT_EDGE",EDGE,{"disambiguationData":[OSD([sQuery(id+"F18.wireOp",EDGE,"E38.bottom"),sQuery(id+"F18.wireOp",EDGE,"E38.left")])]})});
            var Q1;
            Q1=makeQuery(id+"F21.boolean.opBoolean","COPY",EDGE,{"derivedFrom":makeQuery(id+"F21.opExtrude","SWEPT_EDGE",EDGE,{"disambiguationData":[OSD([sQuery(id+"F18.wireOp",EDGE,"E38.bottom"),sQuery(id+"F18.wireOp",EDGE,"E38.right")])]})});
            var Q2;
            Q2=makeQuery(id+"F21.boolean.opBoolean","COPY",EDGE,{"derivedFrom":makeQuery(id+"F21.opExtrude","SWEPT_EDGE",EDGE,{"disambiguationData":[OSD([sQuery(id+"F18.wireOp",EDGE,"E38.top"),sQuery(id+"F18.wireOp",EDGE,"E38.right")])]})});
            var Q3;
            Q3=makeQuery(id+"F21.boolean.opBoolean","COPY",EDGE,{"derivedFrom":makeQuery(id+"F21.opExtrude","SWEPT_EDGE",EDGE,{"disambiguationData":[OSD([sQuery(id+"F18.wireOp",EDGE,"E38.top"),sQuery(id+"F18.wireOp",EDGE,"E38.left")])]})});
            var Q4;
            Q4=makeQuery(id+"F19.boolean.opBoolean","COPY",EDGE,{"derivedFrom":makeQuery(id+"F19.opExtrude","SWEPT_EDGE",EDGE,{"disambiguationData":[OSD([sQuery(id+"F16.wireOp",EDGE,"E36.top"),sQuery(id+"F16.wireOp",EDGE,"E36.left")])]})});
            var Q5;
            Q5=makeQuery(id+"F19.boolean.opBoolean","COPY",EDGE,{"derivedFrom":makeQuery(id+"F19.opExtrude","SWEPT_EDGE",EDGE,{"disambiguationData":[OSD([sQuery(id+"F16.wireOp",EDGE,"E36.top"),sQuery(id+"F16.wireOp",EDGE,"E36.right")])]})});
            var Q6;
            Q6=makeQuery(id+"F19.boolean.opBoolean","COPY",EDGE,{"derivedFrom":makeQuery(id+"F19.opExtrude","SWEPT_EDGE",EDGE,{"disambiguationData":[OSD([sQuery(id+"F16.wireOp",EDGE,"E36.bottom"),sQuery(id+"F16.wireOp",EDGE,"E36.right")])]})});
            var Q7;
            Q7=makeQuery(id+"F19.boolean.opBoolean","COPY",EDGE,{"derivedFrom":makeQuery(id+"F19.opExtrude","SWEPT_EDGE",EDGE,{"disambiguationData":[OSD([sQuery(id+"F16.wireOp",EDGE,"E36.bottom"),sQuery(id+"F16.wireOp",EDGE,"E36.left")])]})});
            var Q8;
            Q8=makeQuery(id+"F15.boolean.opBoolean","COPY",EDGE,{"derivedFrom":makeQuery(id+"F15.opExtrude","SWEPT_EDGE",EDGE,{"disambiguationData":[OSD([sQuery(id+"F12.wireOp",EDGE,"E34.bottom"),sQuery(id+"F12.wireOp",EDGE,"E34.right")])]})});
            var Q9;
            Q9=makeQuery(id+"F15.boolean.opBoolean","COPY",EDGE,{"derivedFrom":makeQuery(id+"F15.opExtrude","SWEPT_EDGE",EDGE,{"disambiguationData":[OSD([sQuery(id+"F12.wireOp",EDGE,"E34.top"),sQuery(id+"F12.wireOp",EDGE,"E34.right")])]})});
            var Q10;
            Q10=makeQuery(id+"F20.boolean.opBoolean","COPY",EDGE,{"derivedFrom":makeQuery(id+"F20.opExtrude","SWEPT_EDGE",EDGE,{"disambiguationData":[OSD([sQuery(id+"F17.wireOp",EDGE,"E37.top"),sQuery(id+"F17.wireOp",EDGE,"E37.left")])]})});
            var Q11;
            Q11=makeQuery(id+"F20.boolean.opBoolean","COPY",EDGE,{"derivedFrom":makeQuery(id+"F20.opExtrude","SWEPT_EDGE",EDGE,{"disambiguationData":[OSD([sQuery(id+"F17.wireOp",EDGE,"E37.bottom"),sQuery(id+"F17.wireOp",EDGE,"E37.left")])]})});
            var Q12;
            Q12=makeQuery(id+"F20.boolean.opBoolean","COPY",EDGE,{"derivedFrom":makeQuery(id+"F20.opExtrude","SWEPT_EDGE",EDGE,{"disambiguationData":[OSD([sQuery(id+"F17.wireOp",EDGE,"E37.top"),sQuery(id+"F17.wireOp",EDGE,"E37.right")])]})});
            var Q13;
            Q13=makeQuery(id+"F20.boolean.opBoolean","COPY",EDGE,{"derivedFrom":makeQuery(id+"F20.opExtrude","SWEPT_EDGE",EDGE,{"disambiguationData":[OSD([sQuery(id+"F17.wireOp",EDGE,"E37.bottom"),sQuery(id+"F17.wireOp",EDGE,"E37.right")])]})});
            var Q14;
            Q14=makeQuery(id+"F13.boolean.opBoolean","COPY",EDGE,{"derivedFrom":makeQuery(id+"F13.opExtrude","SWEPT_EDGE",EDGE,{"disambiguationData":[OSD([sQuery(id+"F10.wireOp",EDGE,"E30.bottom"),sQuery(id+"F10.wireOp",EDGE,"E30.right")])]})});
            var Q15;
            Q15=makeQuery(id+"F13.boolean.opBoolean","COPY",EDGE,{"derivedFrom":makeQuery(id+"F13.opExtrude","SWEPT_EDGE",EDGE,{"disambiguationData":[OSD([sQuery(id+"F10.wireOp",EDGE,"E30.top"),sQuery(id+"F10.wireOp",EDGE,"E30.right")])]})});
            var Q16;
            Q16=makeQuery(id+"F14.boolean.opBoolean","COPY",EDGE,{"derivedFrom":makeQuery(id+"F14.opExtrude","SWEPT_EDGE",EDGE,{"disambiguationData":[OSD([sQuery(id+"F11.wireOp",EDGE,"E32.bottom"),sQuery(id+"F11.wireOp",EDGE,"E32.right")])]})});
            var Q17;
            Q17=makeQuery(id+"F14.boolean.opBoolean","COPY",EDGE,{"derivedFrom":makeQuery(id+"F14.opExtrude","SWEPT_EDGE",EDGE,{"disambiguationData":[OSD([sQuery(id+"F11.wireOp",EDGE,"E32.top"),sQuery(id+"F11.wireOp",EDGE,"E32.right")])]})});
            var Q18;
            Q18=makeQuery(id+"F9.boolean.opBoolean","COPY",EDGE,{"derivedFrom":makeQuery(id+"F9.opExtrude","SWEPT_EDGE",EDGE,{"disambiguationData":[OSD([sQuery(id+"F8.wireOp",EDGE,"E29.1.1"),sQuery(id+"F8.wireOp",EDGE,"E29.1.2")])]})});
            var Q19;
            Q19=makeQuery(id+"F9.boolean.opBoolean","COPY",EDGE,{"derivedFrom":makeQuery(id+"F9.opExtrude","SWEPT_EDGE",EDGE,{"disambiguationData":[OSD([sQuery(id+"F8.wireOp",EDGE,"E29.1.0"),sQuery(id+"F8.wireOp",EDGE,"E29.1.1")])]})});
            var Q20;
            Q20=makeQuery(id+"F9.boolean.opBoolean","COPY",EDGE,{"derivedFrom":makeQuery(id+"F9.opExtrude","SWEPT_EDGE",EDGE,{"disambiguationData":[OSD([sQuery(id+"F8.wireOp",EDGE,"E29.1.0"),sQuery(id+"F8.wireOp",EDGE,"E29.1.3")])]})});
            var Q21;
            Q21=makeQuery(id+"F9.boolean.opBoolean","COPY",EDGE,{"derivedFrom":makeQuery(id+"F9.opExtrude","SWEPT_EDGE",EDGE,{"disambiguationData":[OSD([sQuery(id+"F8.wireOp",EDGE,"E29.1.2"),sQuery(id+"F8.wireOp",EDGE,"E29.1.3")])]})});
            var Q22;
            Q22=makeQuery(id+"F9.boolean.opBoolean","COPY",EDGE,{"derivedFrom":makeQuery(id+"F9.opExtrude","SWEPT_EDGE",EDGE,{"disambiguationData":[OSD([sQuery(id+"F8.wireOp",EDGE,"E29.2.0"),sQuery(id+"F8.wireOp",EDGE,"E29.2.3")])]})});
            var Q23;
            Q23=makeQuery(id+"F9.boolean.opBoolean","COPY",EDGE,{"derivedFrom":makeQuery(id+"F9.opExtrude","SWEPT_EDGE",EDGE,{"disambiguationData":[OSD([sQuery(id+"F8.wireOp",EDGE,"E29.2.0"),sQuery(id+"F8.wireOp",EDGE,"E29.2.1")])]})});
            var Q24;
            Q24=makeQuery(id+"F9.boolean.opBoolean","COPY",EDGE,{"derivedFrom":makeQuery(id+"F9.opExtrude","SWEPT_EDGE",EDGE,{"disambiguationData":[OSD([sQuery(id+"F8.wireOp",EDGE,"E28.top"),sQuery(id+"F8.wireOp",EDGE,"E28.right")])]})});
            var Q25;
            Q25=makeQuery(id+"F9.boolean.opBoolean","COPY",EDGE,{"derivedFrom":makeQuery(id+"F9.opExtrude","SWEPT_EDGE",EDGE,{"disambiguationData":[OSD([sQuery(id+"F8.wireOp",EDGE,"E28.top"),sQuery(id+"F8.wireOp",EDGE,"E28.left")])]})});
            var Q26;
            Q26=makeQuery(id+"F9.boolean.opBoolean","COPY",EDGE,{"derivedFrom":makeQuery(id+"F9.opExtrude","SWEPT_EDGE",EDGE,{"disambiguationData":[OSD([sQuery(id+"F8.wireOp",EDGE,"E29.2.2"),sQuery(id+"F8.wireOp",EDGE,"E29.2.3")])]})});
            var Q27;
            Q27=makeQuery(id+"F9.boolean.opBoolean","COPY",EDGE,{"derivedFrom":makeQuery(id+"F9.opExtrude","SWEPT_EDGE",EDGE,{"disambiguationData":[OSD([sQuery(id+"F8.wireOp",EDGE,"E29.2.1"),sQuery(id+"F8.wireOp",EDGE,"E29.2.2")])]})});
            var Q28;
            Q28=makeQuery(id+"F9.boolean.opBoolean","COPY",EDGE,{"derivedFrom":makeQuery(id+"F9.opExtrude","SWEPT_EDGE",EDGE,{"disambiguationData":[OSD([sQuery(id+"F8.wireOp",EDGE,"E28.bottom"),sQuery(id+"F8.wireOp",EDGE,"E28.right")])]})});
            var Q29;
            Q29=makeQuery(id+"F9.boolean.opBoolean","COPY",EDGE,{"derivedFrom":makeQuery(id+"F9.opExtrude","SWEPT_EDGE",EDGE,{"disambiguationData":[OSD([sQuery(id+"F8.wireOp",EDGE,"E28.bottom"),sQuery(id+"F8.wireOp",EDGE,"E28.left")])]})});
            fillet(context, id + "F26", {"entities" : qUnion([Q0, Q1, Q2, Q3, Q4, Q5, Q6, Q7, Q8, Q9, Q10, Q11, Q12, Q13, Q14, Q15, Q16, Q17, Q18, Q19, Q20, Q21, Q22, Q23, Q24, Q25, Q26, Q27, Q28, Q29]), "tangentPropagation" : true, "radius" : 2 * mm, "defaultsChanged" : false, "vertexSettings" : [], "allowEdgeOverflow" : false});
        }
    });
